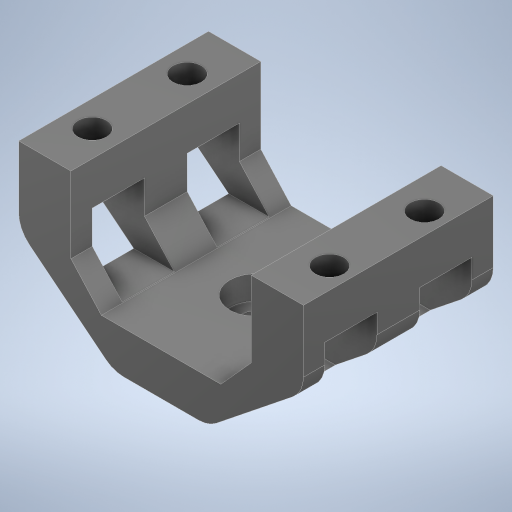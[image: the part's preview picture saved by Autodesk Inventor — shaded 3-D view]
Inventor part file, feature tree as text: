
AUTODESK INVENTOR PART (.ipt)
format: ipt  version: 2024.3 (Build 283343000, 343)  size: 287,744 bytes
history: native  units: in
note: dims shown in document units (in); Inventor stores cm internally (conversion verified against a paired STEP export)
features: extrude x1, sketch x1, other x1
ambient origin geometry x8: Origin, YZ Plane, XZ Plane, XY Plane, X Axis, Y Axis, Z Axis, Center Point
bodies: Solid1 (feature_tree)
feature tree (3):
  extrude  "Extrusion1"  Depth=0.7874in TaperAngle=0.0deg
  sketch  "Sketch1"  dims[d0=0.7874in d2=0.3937in d3=0.7874in d5=0.9843in d8=0.0394in d9=0.0in]
  other  "Cortar-Extruir6"
